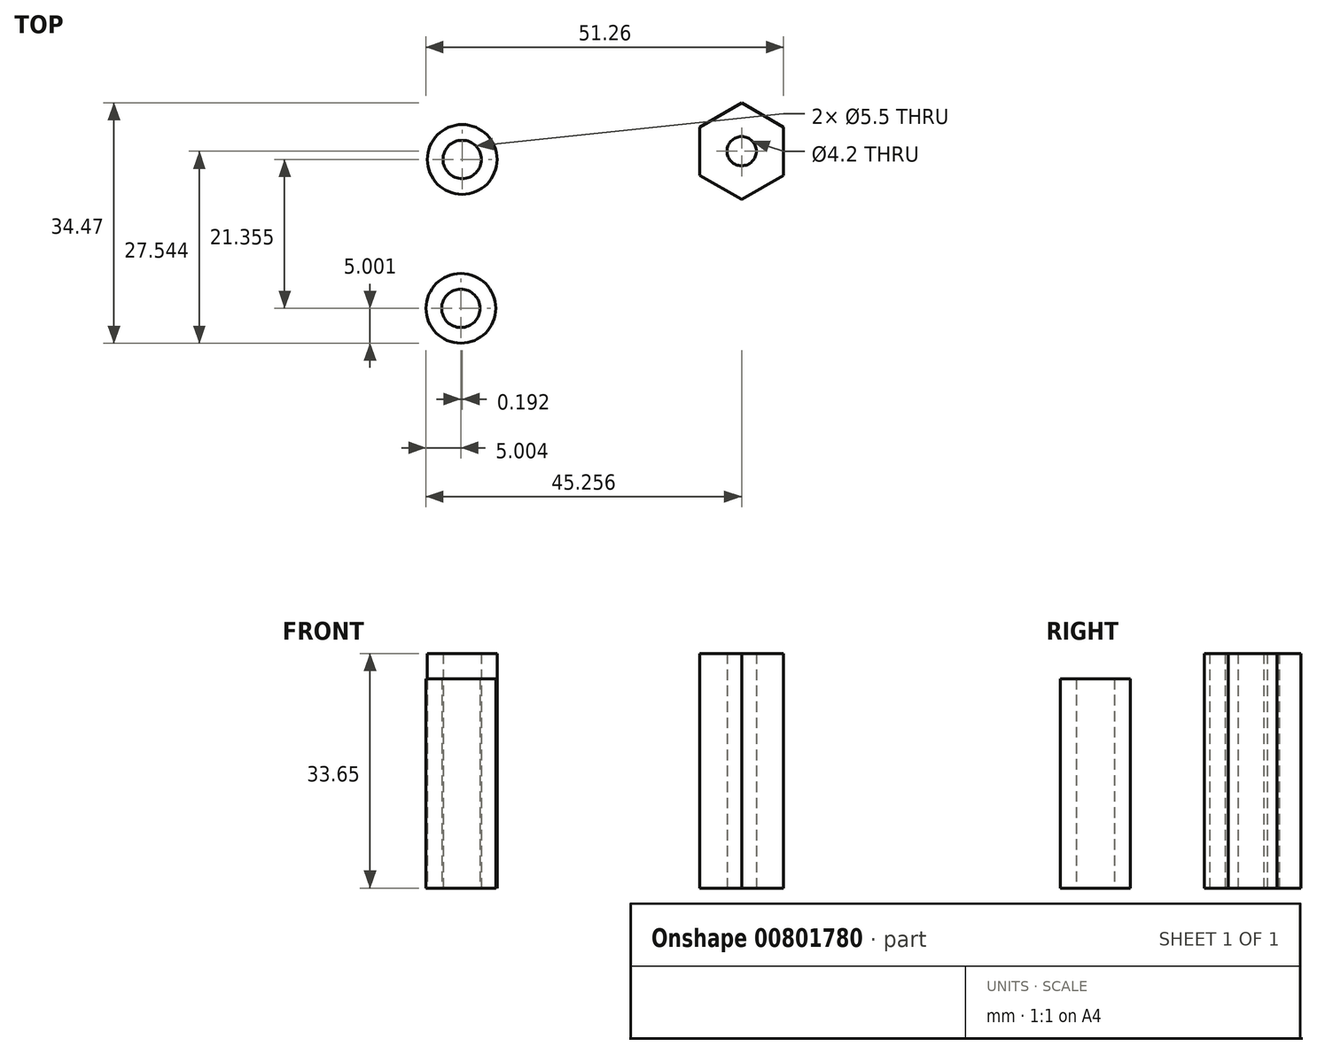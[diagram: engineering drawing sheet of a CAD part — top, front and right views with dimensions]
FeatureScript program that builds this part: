
annotation { "Feature Type Name" : "Feature", "Feature Type Description" : "" }
export const myFeature = defineFeature(function(context is Context, id is Id, definition is map)
    precondition{}
    {
        {
            var Q0;
            Q0=qCreatedBy(makeId("Top.planeOp"),FACE);
            var sketch = newSketch(context, id + "F0", { "sketchPlane" : qUnion([Q0])});
            skCircle(sketch, "E0", {"center": v(-20.3, 15.13) * mm, "radius": 2.75 * mm});
            skCircle(sketch, "E1", {"center": v(-20.3, 15.13) * mm, "radius": 5 * mm});
            skSolve(sketch);
        }
        {
            var Q0;
            Q0=makeQuery(id+"F0.imprint","IMPRINT",FACE,{"disambiguationData":[TD([[makeQuery(id+"F0.imprint","IMPRINT",EDGE,{"derivedFrom":sQuery(id+"F0.wireOp",EDGE,"E0")}),-1.0]])]});
            extrude(context, id + "F1", {"entities" : qUnion([Q0]), "depth" : 33.65 * mm, "offsetDistance" : 25 * mm});
        }
        {
            var Q0;
            Q0=qCreatedBy(makeId("Top.planeOp"),FACE);
            var sketch = newSketch(context, id + "F2", { "sketchPlane" : qUnion([Q0])});
            skCircle(sketch, "E2", {"center": v(-20.49, -6.23) * mm, "radius": 2.75 * mm});
            skCircle(sketch, "E3", {"center": v(-20.49, -6.23) * mm, "radius": 5 * mm});
            skSolve(sketch);
        }
        {
            var Q0;
            Q0=makeQuery(id+"F2.imprint","IMPRINT",FACE,{"disambiguationData":[TD([[makeQuery(id+"F2.imprint","IMPRINT",EDGE,{"derivedFrom":sQuery(id+"F2.wireOp",EDGE,"E2")}),-1.0]])]});
            extrude(context, id + "F3", {"entities" : qUnion([Q0]), "depth" : 30 * mm, "offsetDistance" : 25 * mm});
        }
        {
            var Q0;
            Q0=qCreatedBy(makeId("Top.planeOp"),FACE);
            var sketch = newSketch(context, id + "F4", { "sketchPlane" : qUnion([Q0])});
            skCircle(sketch, "E4", {"center": v(19.77, 16.31) * mm, "radius": 2.1 * mm});
            skCircle(sketch, "E5.cCircle", {"center": v(19.77, 16.31) * mm, "radius": 6 * mm, "construction": true});
            skLineSegment(sketch, "E5.0", {"start": v(25.77, 19.78) * mm, "end": v(25.77, 12.85) * mm});
            skLineSegment(sketch, "E5.1", {"start": v(25.77, 12.85) * mm, "end": v(19.77, 9.39) * mm});
            skLineSegment(sketch, "E5.2", {"start": v(19.77, 9.39) * mm, "end": v(13.77, 12.85) * mm});
            skLineSegment(sketch, "E5.3", {"start": v(13.77, 12.85) * mm, "end": v(13.77, 19.78) * mm});
            skLineSegment(sketch, "E5.4", {"start": v(13.77, 19.78) * mm, "end": v(19.77, 23.24) * mm});
            skLineSegment(sketch, "E5.5", {"start": v(19.77, 23.24) * mm, "end": v(25.77, 19.78) * mm});
            skPoint(sketch, "E5.0.midPoint", {"position": v(25.77, 16.31) * mm});
            skSolve(sketch);
        }
        {
            var Q0;
            Q0=makeQuery(id+"F4.imprint","IMPRINT",FACE,{"disambiguationData":[TD([[makeQuery(id+"F4.imprint","IMPRINT",EDGE,{"derivedFrom":sQuery(id+"F4.wireOp",EDGE,"E4")}),-1.0]])]});
            extrude(context, id + "F5", {"entities" : qUnion([Q0]), "depth" : 33.65 * mm, "offsetDistance" : 25 * mm});
        }
    });
